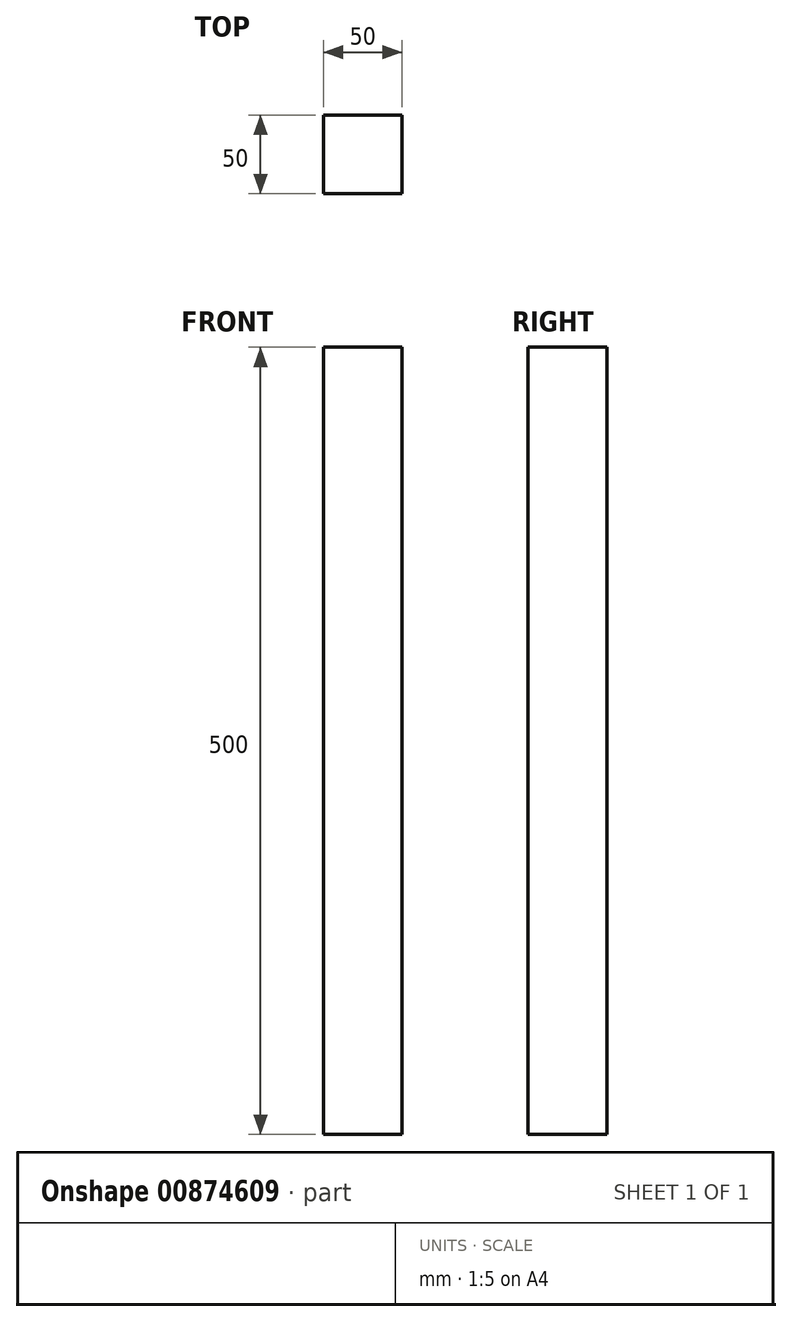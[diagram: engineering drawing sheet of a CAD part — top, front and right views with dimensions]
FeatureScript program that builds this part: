
annotation { "Feature Type Name" : "Feature", "Feature Type Description" : "" }
export const myFeature = defineFeature(function(context is Context, id is Id, definition is map)
    precondition{}
    {
        {
            var Q0;
            Q0=qCreatedBy(makeId("Top.planeOp"),FACE);
            var sketch = newSketch(context, id + "F0", { "sketchPlane" : qUnion([Q0])});
            skLineSegment(sketch, "E0.bottom", {"start": v(0, 0) * mm, "end": v(50, 0) * mm});
            skLineSegment(sketch, "E0.top", {"start": v(0, 50) * mm, "end": v(50, 50) * mm});
            skLineSegment(sketch, "E0.left", {"start": v(0, 0) * mm, "end": v(0, 50) * mm});
            skLineSegment(sketch, "E0.right", {"start": v(50, 0) * mm, "end": v(50, 50) * mm});
            skSolve(sketch);
        }
        {
            var Q0;
            Q0 = qSketchRegion(id + "F0", true);
            extrude(context, id + "F1", {"entities" : qUnion([Q0]), "depth" : 500 * mm, "offsetDistance" : 25 * mm});
        }
    });
